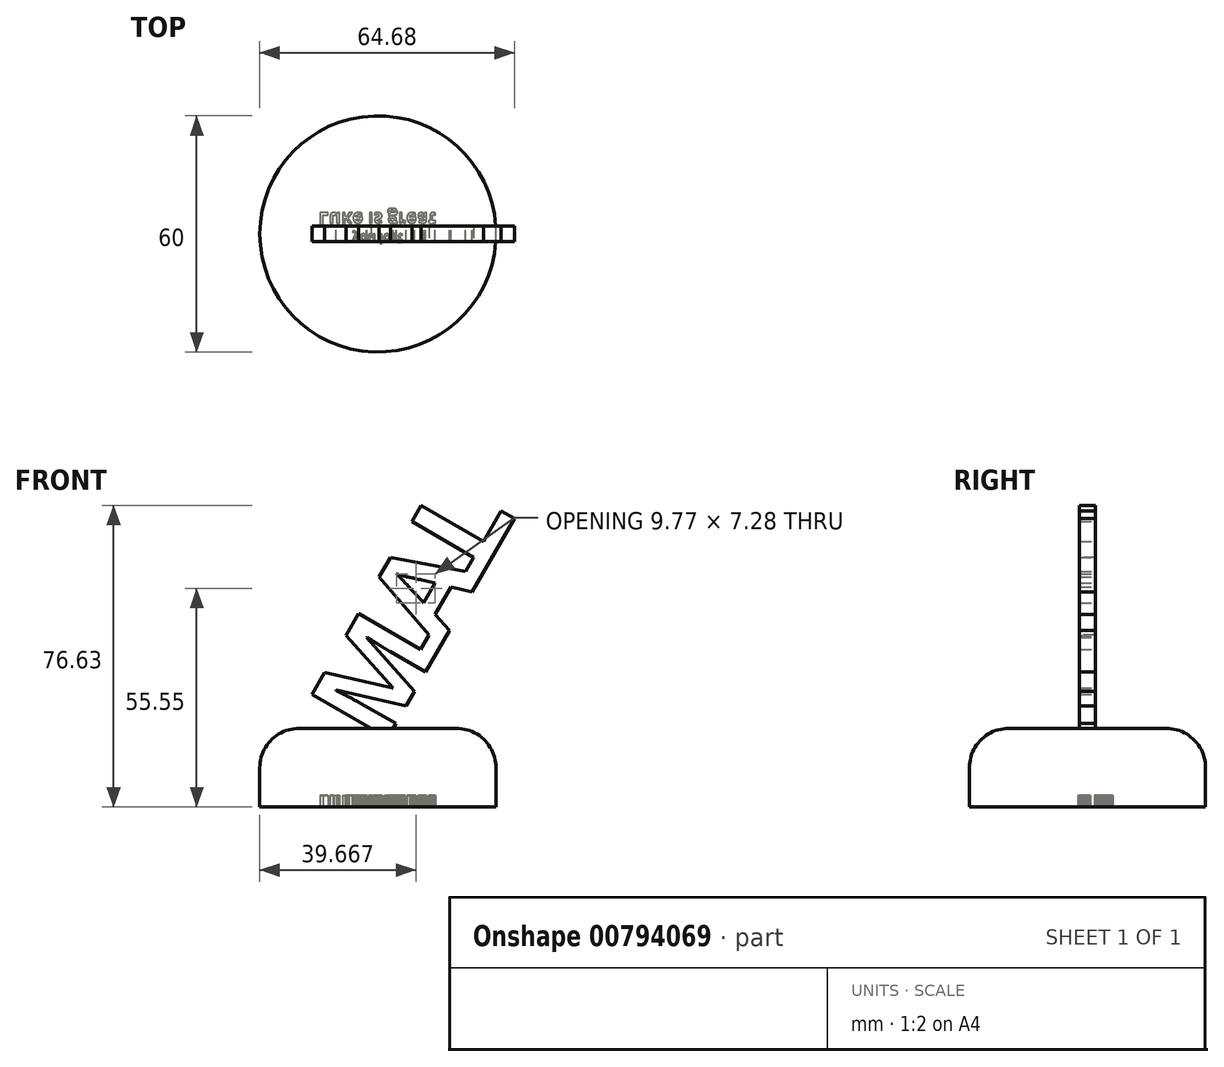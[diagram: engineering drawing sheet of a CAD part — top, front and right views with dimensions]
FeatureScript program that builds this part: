
annotation { "Feature Type Name" : "Feature", "Feature Type Description" : "" }
export const myFeature = defineFeature(function(context is Context, id is Id, definition is map)
    precondition{}
    {
        {
            var Q0;
            Q0=qCreatedBy(makeId("Top.planeOp"),FACE);
            var sketch = newSketch(context, id + "F0", { "sketchPlane" : qUnion([Q0])});
            skCircle(sketch, "E0", {"center": v(0, 0) * mm, "radius": 30 * mm});
            skSolve(sketch);
        }
        {
            var Q0;
            Q0=makeQuery(id+"F0.imprint","IMPRINT",FACE,{"disambiguationData":[TD([[makeQuery(id+"F0.imprint","IMPRINT",EDGE,{"derivedFrom":sQuery(id+"F0.wireOp",EDGE,"E0")}),1.0]])]});
            extrude(context, id + "F1", {"entities" : qUnion([Q0]), "depth" : 20 * mm, "offsetDistance" : 25 * mm});
        }
        {
            var Q0;
            Q0=makeQuery(id+"F1.opExtrude","CAP_EDGE",EDGE,{"disambiguationData":[OSD([sQuery(id+"F0.wireOp",EDGE,"E0")])],"isStart":false});
            fillet(context, id + "F2", {"entities" : qUnion([Q0]), "radius" : 10 * mm, "tangentPropagation" : true, "allowEdgeOverflow" : false});
        }
        {
            var Q0;
            Q0=qCreatedBy(makeId("Front.planeOp"),FACE);
            var sketch = newSketch(context, id + "F3", { "sketchPlane" : qUnion([Q0])});
            skText(sketch, "E1", { "text": "MAL", "fontName": "OpenSans-Bold.ttf"});
            const initialGuessF3  = {"E1": [0.00108, 0.01514, 0.5, 0.86603, 0.02236]};
            skSetInitialGuess(sketch, initialGuessF3);
            skSolve(sketch);
        }
        {
            var Q0;
            Q0 = qSketchRegion(id + "F3", true);
            extrude(context, id + "F4", {"entities" : qUnion([Q0]), "operationType" : NewBodyOperationType.ADD, "endBound" : BoundingType.SYMMETRIC, "depth" : 4 * mm, "offsetDistance" : 25 * mm});
        }
        {
            var Q0;
            Q0=makeQuery(id+"F4.opExtrude","SWEPT_FACE",FACE,{"disambiguationData":[OSD([sQuery(id+"F3.wireOp",EDGE,"E1.sketch_text.stroke-36")])]});
            var sketch = newSketch(context, id + "F5", { "sketchPlane" : qUnion([Q0])});
            skLineSegment(sketch, "E2.bottom", {"start": v(-2, 71.1) * mm, "end": v(2, 71.1) * mm});
            skLineSegment(sketch, "E2.top", {"start": v(-2, 61.96) * mm, "end": v(2, 61.96) * mm});
            skLineSegment(sketch, "E2.left", {"start": v(-2, 71.1) * mm, "end": v(-2, 61.96) * mm});
            skLineSegment(sketch, "E2.right", {"start": v(2, 71.1) * mm, "end": v(2, 61.96) * mm});
            skSolve(sketch);
        }
        {
            var Q0;
            {var subQ0=sQuery(id+"F5.wireOp",EDGE,"E2.top");Q0=makeQuery(id+"F5.imprint","IMPRINT",FACE,{"disambiguationData":[TD([[makeQuery(id+"F5.imprint","IMPRINT",EDGE,{"derivedFrom":subQ0}),1.0]])]});}
            var Q1;
            {var subQ0=sQuery(id+"F5.wireOp",EDGE,"E2.bottom");Q1=makeQuery(id+"F5.imprint","IMPRINT",FACE,{"disambiguationData":[TD([[makeQuery(id+"F5.imprint","IMPRINT",EDGE,{"derivedFrom":subQ0}),-1.0]])]});}
            extrude(context, id + "F6", {"entities" : qUnion([Q0, Q1]), "operationType" : NewBodyOperationType.ADD, "oppositeDirection" : true, "depth" : 4 * mm, "offsetDistance" : 25 * mm});
        }
        {
            var Q0;
            Q0=makeQuery(id+"F4.opExtrude","SWEPT_FACE",FACE,{"disambiguationData":[OSD([sQuery(id+"F3.wireOp",EDGE,"E1.sketch_text.stroke-12")])]});
            var sketch = newSketch(context, id + "F7", { "sketchPlane" : qUnion([Q0])});
            skLineSegment(sketch, "E3.bottom", {"start": v(-2, 37.95) * mm, "end": v(2, 37.95) * mm});
            skLineSegment(sketch, "E3.top", {"start": v(-2, 45.32) * mm, "end": v(2, 45.32) * mm});
            skLineSegment(sketch, "E3.left", {"start": v(-2, 37.95) * mm, "end": v(-2, 45.32) * mm});
            skLineSegment(sketch, "E3.right", {"start": v(2, 37.95) * mm, "end": v(2, 45.32) * mm});
            skSolve(sketch);
        }
        {
            var Q0;
            Q0 = qSketchRegion(id + "F7", true);
            extrude(context, id + "F8", {"entities" : qUnion([Q0]), "operationType" : NewBodyOperationType.ADD, "oppositeDirection" : true, "depth" : 4 * mm, "offsetDistance" : 25 * mm});
        }
        {
            var Q0;
            Q0=makeQuery(id+"F1.opExtrude","CAP_FACE",FACE,{"disambiguationData":[OSD([sQuery(id+"F0.wireOp",EDGE,"E0")])],"isStart":true});
            var sketch = newSketch(context, id + "F9", { "sketchPlane" : qUnion([Q0])});
            skText(sketch, "E4", { "text": "you lost", "fontName": "OpenSans-Bold.ttf"});
            skText(sketch, "E5", { "text": "Luke is great", "fontName": "OpenSans-Bold.ttf"});
            const initialGuessF9  = {"E4": [-0.00652, 0, 1, 0, 0.00234], "E5": [-0.01508, -0.00536, 1, 0, 0.00336]};
            skSetInitialGuess(sketch, initialGuessF9);
            skSolve(sketch);
        }
        {
            var Q0;
            Q0 = qSketchRegion(id + "F9", true);
            extrude(context, id + "F10", {"entities" : qUnion([Q0]), "operationType" : NewBodyOperationType.REMOVE, "oppositeDirection" : true, "depth" : 3 * mm, "offsetDistance" : 25 * mm});
        }
    });
